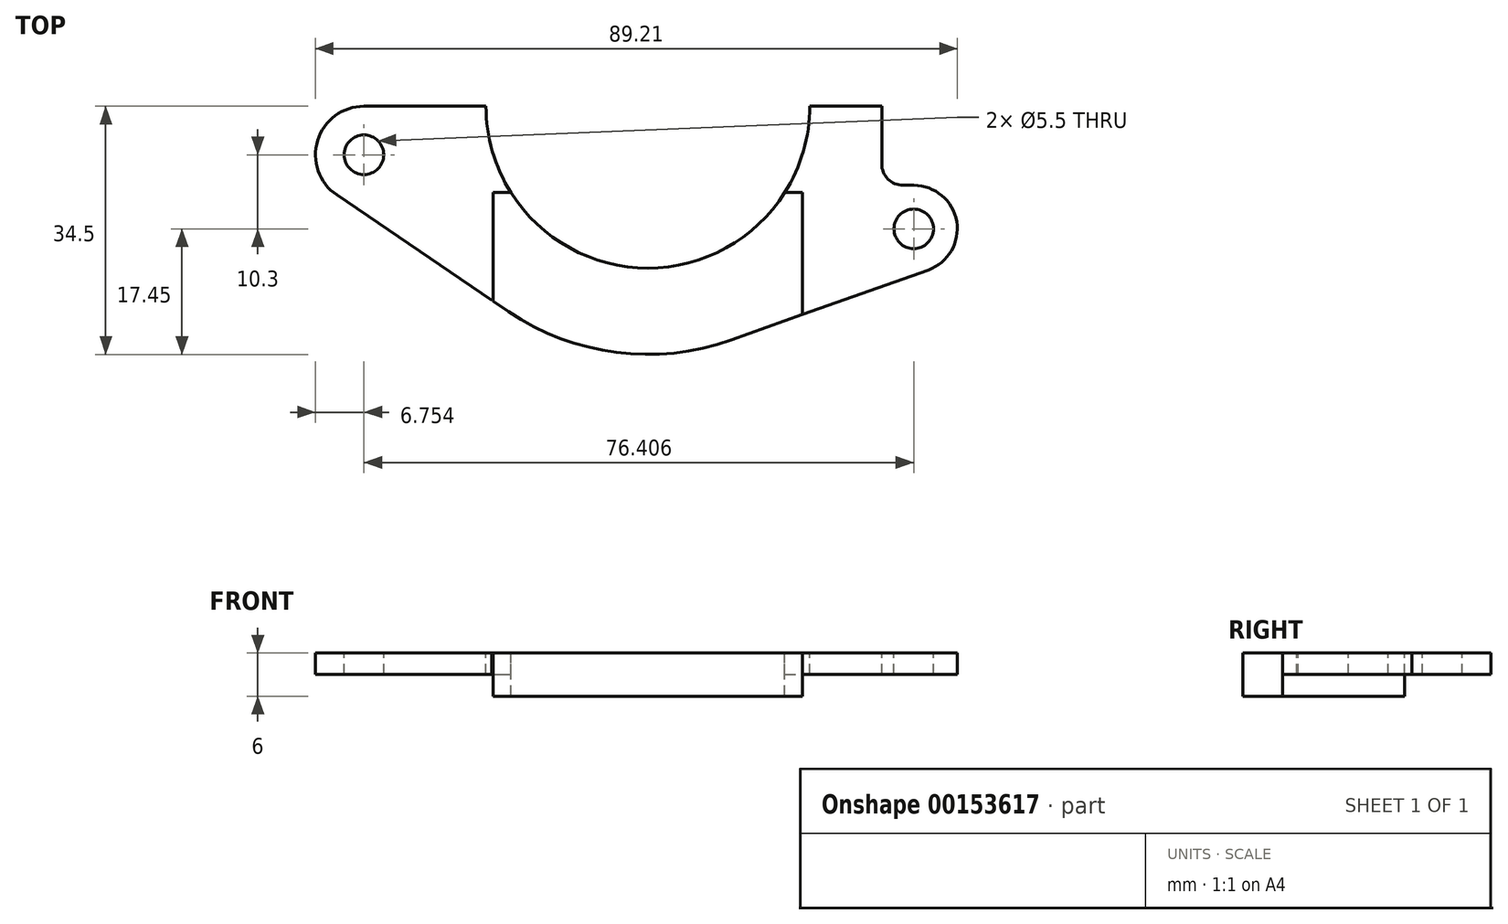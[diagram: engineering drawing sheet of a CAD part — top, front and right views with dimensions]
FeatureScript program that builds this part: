
annotation { "Feature Type Name" : "Feature", "Feature Type Description" : "" }
export const myFeature = defineFeature(function(context is Context, id is Id, definition is map)
    precondition{}
    {
        {
            var Q0;
            Q0=qCreatedBy(makeId("Top.planeOp"),FACE);
            var sketch = newSketch(context, id + "F0", { "sketchPlane" : qUnion([Q0])});
            skArc(sketch, "E0", {"start": v(-22.5, 0) * mm, "mid": v(0, -22.5) * mm, "end": v(22.5, 0) * mm});
            skArc(sketch, "E1.0", {"start": v(-34.5, 0) * mm, "mid": v(-5.57, -34.05) * mm, "end": v(32.7, -11) * mm});
            skLineSegment(sketch, "E2", {"start": v(-34.5, 0) * mm, "end": v(-22.5, 0) * mm});
            skLineSegment(sketch, "E3", {"start": v(22.5, 0) * mm, "end": v(32.5, 0) * mm});
            skCircle(sketch, "E4", {"center": v(-39.46, -6.75) * mm, "radius": 2.75 * mm});
            skCircle(sketch, "E5.0", {"center": v(-39.46, -6.75) * mm, "radius": 6.75 * mm});
            skLineSegment(sketch, "E6", {"start": v(-34.5, 0) * mm, "end": v(-39.46, 0) * mm});
            skLineSegment(sketch, "E7", {"start": v(-43.25, -12.33) * mm, "end": v(-19.38, -28.54) * mm});
            skCircle(sketch, "E8", {"center": v(36.95, -17.05) * mm, "radius": 2.75 * mm});
            skPoint(sketch, "E9.visualSharp", {"position": v(34.5, -11) * mm});
            skLineSegment(sketch, "E10", {"start": v(-21.7, -26.97) * mm, "end": v(-21.7, -26.82) * mm});
            skLineSegment(sketch, "E11", {"start": v(21.5, -29.98) * mm, "end": v(21.5, 3.02) * mm});
            skPoint(sketch, "E12.trimOffspring.end.orphan", {"position": v(-22.5, 4.82) * mm});
            skLineSegment(sketch, "E13.MirrorCS", {"start": v(-21.5, -27.1) * mm, "end": v(-21.5, -12) * mm});
            skPoint(sketch, "E14", {"position": v(-21.5, -12) * mm});
            skLineSegment(sketch, "E15", {"start": v(-21.5, -12) * mm, "end": v(-19.03, -12) * mm});
            skLineSegment(sketch, "E16.trimOffspring", {"start": v(19.03, -12) * mm, "end": v(21.5, -12) * mm});
            skPoint(sketch, "E17.orphan", {"position": v(-21.5, -34.5) * mm});
            skPoint(sketch, "E18.start.orphan", {"position": v(0, -34.5) * mm});
            skPoint(sketch, "E19.orphan", {"position": v(21.5, -34.5) * mm});
            skPoint(sketch, "E20.orphan", {"position": v(-21.5, 3.02) * mm});
            skPoint(sketch, "E21", {"position": v(32.5, 0) * mm});
            skLineSegment(sketch, "E22", {"start": v(32.5, 0) * mm, "end": v(32.5, -8) * mm});
            skLineSegment(sketch, "E23", {"start": v(35.5, -11) * mm, "end": v(36.95, -11) * mm});
            skCircle(sketch, "E24.0", {"center": v(36.95, -17.05) * mm, "radius": 6.05 * mm});
            skLineSegment(sketch, "E25", {"start": v(11.57, -32.5) * mm, "end": v(38.98, -22.75) * mm});
            skPoint(sketch, "E26.orphan", {"position": v(34.5, 0) * mm});
            skPoint(sketch, "E27.visualSharp", {"position": v(32.5, -11) * mm});
            skArc(sketch, "E27.filletArc", {"start": v(32.5, -8) * mm, "mid": v(33.38, -10.12) * mm, "end": v(35.5, -11) * mm});
            skSolve(sketch);
        }
        {
            var Q0;
            Q0=makeQuery(id+"F0.imprint","IMPRINT",FACE,{"disambiguationData":[TD([[makeQuery(id+"F0.imprint","IMPRINT",EDGE,{"derivedFrom":sQuery(id+"F0.wireOp",EDGE,"E4")}),-1.0]])]});
            var Q1;
            {var subQ0=sQuery(id+"F0.wireOp",EDGE,"E10");Q1=makeQuery(id+"F0.imprint","IMPRINT",FACE,{"disambiguationData":[TD([[makeQuery(id+"F0.imprint","IMPRINT",EDGE,{"derivedFrom":subQ0}),1.0]])]});}
            var Q2;
            {var subQ0=sQuery(id+"F0.wireOp",EDGE,"E5.0");var subQ1=sQuery(id+"F0.wireOp",EDGE,"E1.0");var subQ2=makeQuery(id+"F0.imprint","INTERSECT",VERTEX,{"disambiguationData":[OD(0.0)],"derivedFrom":[subQ1,subQ0]});Q2=makeQuery(id+"F0.imprint","IMPRINT",FACE,{"disambiguationData":[TD([[makeQuery(id+"F0.imprint","IMPRINT",EDGE,{"disambiguationData":[TD([[subQ2,-1.0]])],"derivedFrom":subQ1}),1.0]])]});}
            var Q3;
            {var subQ0=sQuery(id+"F0.wireOp",EDGE,"E6");Q3=makeQuery(id+"F0.imprint","IMPRINT",FACE,{"disambiguationData":[TD([[makeQuery(id+"F0.imprint","IMPRINT",EDGE,{"derivedFrom":subQ0}),1.0]])]});}
            var Q4;
            {var subQ8=sQuery(id+"F0.wireOp",EDGE,"E2");Q4=makeQuery(id+"F0.imprint","IMPRINT",FACE,{"disambiguationData":[TD([[makeQuery(id+"F0.imprint","IMPRINT",EDGE,{"derivedFrom":subQ8}),-1.0]])]});}
            var Q5;
            {var subQ0=sQuery(id+"F0.wireOp",EDGE,"E3");Q5=makeQuery(id+"F0.imprint","IMPRINT",FACE,{"disambiguationData":[TD([[makeQuery(id+"F0.imprint","IMPRINT",EDGE,{"derivedFrom":subQ0}),-1.0]])]});}
            var Q6;
            {var subQ1=sQuery(id+"F0.wireOp",EDGE,"zKS9e9Rl-YkTg-wg0Q-Oahr-Ui1y3zF19yGP");Q6=makeQuery(id+"F0.imprint","IMPRINT",FACE,{"disambiguationData":[TD([[makeQuery(id+"F0.imprint","IMPRINT",EDGE,{"derivedFrom":subQ1}),-1.0]])]});}
            var Q7;
            Q7=makeQuery(id+"F0.imprint","IMPRINT",FACE,{"disambiguationData":[TD([[makeQuery(id+"F0.imprint","IMPRINT",EDGE,{"derivedFrom":sQuery(id+"F0.wireOp",EDGE,"E8")}),-1.0]])]});
            var Q8;
            {var subQ0=sQuery(id+"F0.wireOp",EDGE,"E16.trimOffspring");Q8=makeQuery(id+"F0.imprint","IMPRINT",FACE,{"disambiguationData":[TD([[makeQuery(id+"F0.imprint","IMPRINT",EDGE,{"derivedFrom":subQ0}),1.0]])]});}
            extrude(context, id + "F1", {"entities" : qUnion([Q0, Q1, Q2, Q3, Q4, Q5, Q6, Q7, Q8]), "oppositeDirection" : true, "depth" : 3 * mm});
        }
        {
            var Q0;
            {var subQ8=sQuery(id+"F0.wireOp",EDGE,"E15");Q0=makeQuery(id+"F0.imprint","IMPRINT",FACE,{"disambiguationData":[TD([[makeQuery(id+"F0.imprint","IMPRINT",EDGE,{"derivedFrom":subQ8}),-1.0]])]});}
            var Q1;
            {var subQ0=sQuery(id+"F0.wireOp",EDGE,"x4Rgk0o0-gJAR-aotj-Jdca-hT2mFVKmOBSV");var subQ1=sQuery(id+"F0.wireOp",EDGE,"E1.0");var subQ2=makeQuery(id+"F0.imprint","INTERSECT",VERTEX,{"derivedFrom":[subQ1,subQ0]});Q1=makeQuery(id+"F0.imprint","IMPRINT",FACE,{"disambiguationData":[TD([[makeQuery(id+"F0.imprint","IMPRINT",EDGE,{"disambiguationData":[TD([[subQ2,-1.0]])],"derivedFrom":subQ1}),-1.0]])]});}
            extrude(context, id + "F2", {"entities" : qUnion([Q0, Q1]), "oppositeDirection" : true, "depth" : 6 * mm});
        }
    });
